# Revit family: DOMO SENSIA UE Pila
name_source: partatom
category: Aparatos sanitarios
revit_build: Autodesk Revit 2015 (Build: 20140223_1515(x64)
units: mm (PartAtom-declared; Revit-internal decimal feet)

## types (1)
- 79600
    CAUDAL = 1 L/Min
    Comentarios de tipo = ◦Descarga de 4 seg después de que el usuario haya abandonado el urinario
◦Proceso automático de adaptación al medio
Pack de batería estanco IP65 compuesto por una batería de 6 V
◦Indicación de batería baja mediante LED de comunicación
◦Presión de uso recomendada: 1-5 bar (min, 08 – max 8 bar)
◦Ahorro de agua y energía
◦Componentes integrados: mantenimiento sencillo y excelente estanqueidad
◦Conexiones internas estancas
◦Cierre automático en caso de pila agotada
◦Aclarado automático cada 24h
◦Suministrado con: Batería CPR2
◦Sistema de fijación antivandálico con placa intermedia
◦Transformacion
    Conexión AC = Sí
    Conexión AF = Sí
    Código de montaje = C1030220
    Descripción = Grifo electrónico para urinario, fijación mural.
    ENTRADA = Macho 1/2"
    Elevación por defecto = 1219 mm
    Fabricante = PRESTO IBÉRICA
    Imagen de tipo = <Ninguno>
    Material = Presto Ibérica: LATON NIQUELADO
    Modelo = PRESTO DOMO SENSIA UE
    PESO BRUTO = 0.750 Kg
    Presión Máxima = 8 bar
    REFERENCIA = 79600
    Teléfono = (+34) 915 782 575
    URL = http://www.prestoiberica.com
